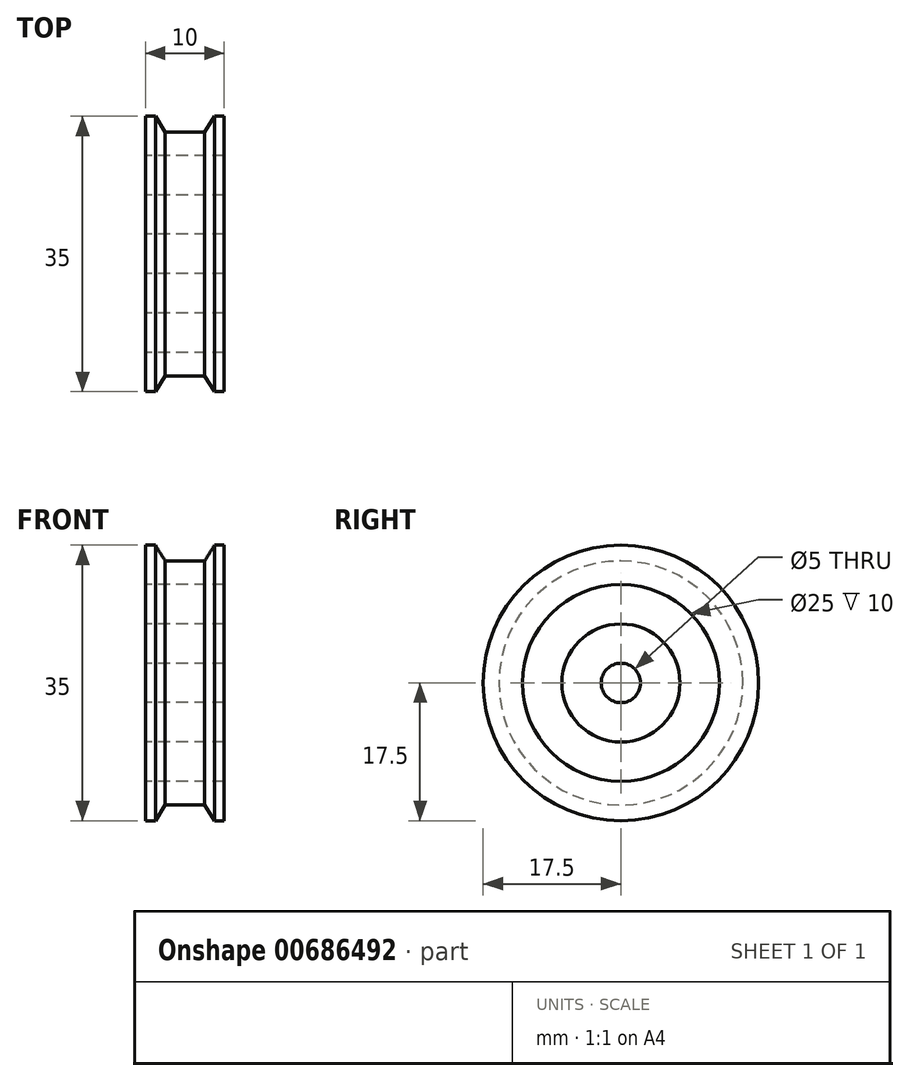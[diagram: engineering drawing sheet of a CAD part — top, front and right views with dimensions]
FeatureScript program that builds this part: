
annotation { "Feature Type Name" : "Feature", "Feature Type Description" : "" }
export const myFeature = defineFeature(function(context is Context, id is Id, definition is map)
    precondition{}
    {
        {
            var Q0;
            Q0=qCreatedBy(makeId("Front.planeOp"),FACE);
            var sketch = newSketch(context, id + "F0", { "sketchPlane" : qUnion([Q0])});
            skLineSegment(sketch, "E0.bottom", {"start": v(-5, 0) * mm, "end": v(5, 0) * mm});
            skLineSegment(sketch, "E0.top", {"start": v(-5, 5) * mm, "end": v(5, 5) * mm});
            skLineSegment(sketch, "E0.left", {"start": v(-5, 0) * mm, "end": v(-5, 5) * mm});
            skLineSegment(sketch, "E0.right", {"start": v(5, 0) * mm, "end": v(5, 5) * mm});
            skLineSegment(sketch, "E1.bottom", {"start": v(-2.5, 5) * mm, "end": v(2.5, 5) * mm});
            skLineSegment(sketch, "E1.top", {"start": v(-2.5, 10) * mm, "end": v(2.5, 10) * mm});
            skLineSegment(sketch, "E2.bottom", {"start": v(-5, 10) * mm, "end": v(5, 10) * mm});
            skLineSegment(sketch, "E2.left", {"start": v(-5, 10) * mm, "end": v(-5, 15) * mm});
            skLineSegment(sketch, "E2.right", {"start": v(5, 10) * mm, "end": v(5, 15) * mm});
            skLineSegment(sketch, "E3", {"start": v(-2.5, 13) * mm, "end": v(2.5, 13) * mm});
            skLineSegment(sketch, "E4", {"start": v(-10.08, -2.5) * mm, "end": v(13.09, -2.5) * mm});
            skLineSegment(sketch, "E5", {"start": v(-5, 10) * mm, "end": v(-5, 5) * mm});
            skLineSegment(sketch, "E6", {"start": v(5, 10) * mm, "end": v(5, 5) * mm});
            skLineSegment(sketch, "E7", {"start": v(-5, 15) * mm, "end": v(-3.75, 15) * mm});
            skLineSegment(sketch, "E8", {"start": v(-3.75, 15) * mm, "end": v(-2.5, 13) * mm});
            skLineSegment(sketch, "E9", {"start": v(5, 15) * mm, "end": v(3.75, 15) * mm});
            skLineSegment(sketch, "E10", {"start": v(3.75, 15) * mm, "end": v(2.5, 13) * mm});
            skSolve(sketch);
        }
        {
            var Q0;
            Q0=makeQuery(id+"F0.imprint","IMPRINT",FACE,{"disambiguationData":[TD([[makeQuery(id+"F0.imprint","IMPRINT",EDGE,{"derivedFrom":sQuery(id+"F0.wireOp",EDGE,"E1.bottom")}),1.0]])]});
            var Q1;
            {var subQ0=sQuery(id+"F0.wireOp",EDGE,"E2.left");Q1=makeQuery(id+"F0.imprint","IMPRINT",FACE,{"disambiguationData":[TD([[makeQuery(id+"F0.imprint","IMPRINT",EDGE,{"derivedFrom":subQ0}),-1.0]])]});}
            var Q2;
            Q2=makeQuery(id+"F0.imprint","IMPRINT",FACE,{"disambiguationData":[TD([[makeQuery(id+"F0.imprint","IMPRINT",EDGE,{"derivedFrom":sQuery(id+"F0.wireOp",EDGE,"E0.bottom")}),1.0]])]});
            var Q3;
            Q3=sQuery(id+"F0.wireOp",EDGE,"E4");
            revolve(context, id + "F1", {"entities" : qUnion([Q0, Q1, Q2]), "axis" : qUnion([Q3]), "revolveType" : RevolveType.FULL});
        }
    });
